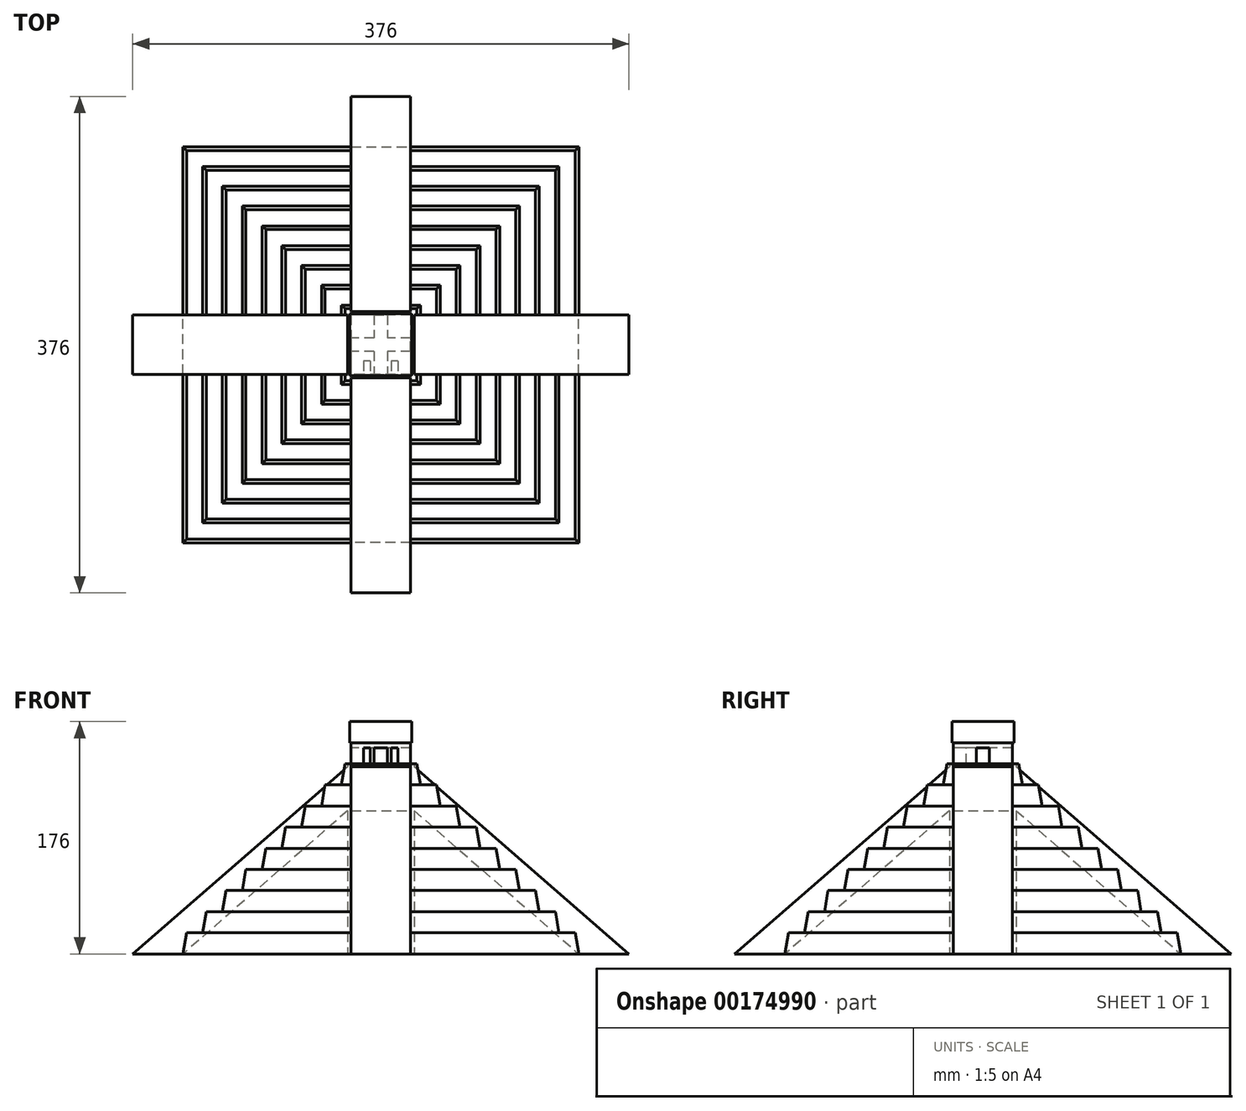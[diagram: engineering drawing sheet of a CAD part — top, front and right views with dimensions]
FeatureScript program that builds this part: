
annotation { "Feature Type Name" : "Feature", "Feature Type Description" : "" }
export const myFeature = defineFeature(function(context is Context, id is Id, definition is map)
    precondition{}
    {
        {
            var Q0;
            Q0=qCreatedBy(makeId("Top.planeOp"),FACE);
            var sketch = newSketch(context, id + "F0", { "sketchPlane" : qUnion([Q0])});
            skLineSegment(sketch, "E0.bottom", {"start": v(150, 150) * mm, "end": v(-150, 150) * mm});
            skLineSegment(sketch, "E0.top", {"start": v(150, -150) * mm, "end": v(-150, -150) * mm});
            skLineSegment(sketch, "E0.left", {"start": v(150, 150) * mm, "end": v(150, -150) * mm});
            skLineSegment(sketch, "E0.right", {"start": v(-150, 150) * mm, "end": v(-150, -150) * mm});
            skPoint(sketch, "E0.middle", {"position": v(0, 0) * mm});
            skSolve(sketch);
        }
        {
            var Q0;
            Q0=makeQuery(id+"F0.imprint","IMPRINT",FACE,{"disambiguationData":[TD([[makeQuery(id+"F0.imprint","IMPRINT",EDGE,{"derivedFrom":sQuery(id+"F0.wireOp",EDGE,"E0.bottom")}),1.0]])]});
            extrude(context, id + "F1", {"entities" : qUnion([Q0]), "depth" : 16 * mm, "hasDraft" : true, "draftAngle" : 10 * degree, "draftPullDirection" : true});
        }
        {
            var Q0;
            Q0=makeQuery(id+"F1.opExtrude","CAP_FACE",FACE,{"disambiguationData":[OSD([sQuery(id+"F0.wireOp",EDGE,"E0.bottom"),sQuery(id+"F0.wireOp",EDGE,"E0.top"),sQuery(id+"F0.wireOp",EDGE,"E0.left"),sQuery(id+"F0.wireOp",EDGE,"E0.right")])],"isStart":false});
            var sketch = newSketch(context, id + "F2", { "sketchPlane" : qUnion([Q0])});
            skLineSegment(sketch, "E1.bottom", {"start": v(135, 135) * mm, "end": v(-135, 135) * mm});
            skLineSegment(sketch, "E1.top", {"start": v(135, -135) * mm, "end": v(-135, -135) * mm});
            skLineSegment(sketch, "E1.left", {"start": v(135, 135) * mm, "end": v(135, -135) * mm});
            skLineSegment(sketch, "E1.right", {"start": v(-135, 135) * mm, "end": v(-135, -135) * mm});
            skPoint(sketch, "E1.middle", {"position": v(0, 0) * mm});
            skSolve(sketch);
        }
        {
            var Q0;
            Q0=makeQuery(id+"F2.imprint","IMPRINT",FACE,{"disambiguationData":[TD([[makeQuery(id+"F2.imprint","IMPRINT",EDGE,{"derivedFrom":sQuery(id+"F2.wireOp",EDGE,"E1.bottom")}),1.0]])]});
            extrude(context, id + "F3", {"entities" : qUnion([Q0]), "operationType" : NewBodyOperationType.ADD, "depth" : 16 * mm, "hasDraft" : true, "draftAngle" : 10 * degree, "draftPullDirection" : true});
        }
        {
            var Q0;
            Q0=makeQuery(id+"F3.opExtrude","CAP_FACE",FACE,{"disambiguationData":[OSD([sQuery(id+"F2.wireOp",EDGE,"E1.bottom"),sQuery(id+"F2.wireOp",EDGE,"E1.top"),sQuery(id+"F2.wireOp",EDGE,"E1.left"),sQuery(id+"F2.wireOp",EDGE,"E1.right")])],"isStart":false});
            var sketch = newSketch(context, id + "F4", { "sketchPlane" : qUnion([Q0])});
            skLineSegment(sketch, "E2.bottom", {"start": v(120, 120) * mm, "end": v(-120, 120) * mm});
            skLineSegment(sketch, "E2.top", {"start": v(120, -120) * mm, "end": v(-120, -120) * mm});
            skLineSegment(sketch, "E2.left", {"start": v(120, 120) * mm, "end": v(120, -120) * mm});
            skLineSegment(sketch, "E2.right", {"start": v(-120, 120) * mm, "end": v(-120, -120) * mm});
            skPoint(sketch, "E2.middle", {"position": v(0, 0) * mm});
            skSolve(sketch);
        }
        {
            var Q0;
            Q0=makeQuery(id+"F4.imprint","IMPRINT",FACE,{"disambiguationData":[TD([[makeQuery(id+"F4.imprint","IMPRINT",EDGE,{"derivedFrom":sQuery(id+"F4.wireOp",EDGE,"E2.bottom")}),1.0]])]});
            extrude(context, id + "F5", {"entities" : qUnion([Q0]), "operationType" : NewBodyOperationType.ADD, "depth" : 16 * mm, "hasDraft" : true, "draftAngle" : 10 * degree, "draftPullDirection" : true});
        }
        {
            var Q0;
            Q0=makeQuery(id+"F5.opExtrude","CAP_FACE",FACE,{"disambiguationData":[OSD([sQuery(id+"F4.wireOp",EDGE,"E2.bottom"),sQuery(id+"F4.wireOp",EDGE,"E2.top"),sQuery(id+"F4.wireOp",EDGE,"E2.left"),sQuery(id+"F4.wireOp",EDGE,"E2.right")])],"isStart":false});
            var sketch = newSketch(context, id + "F6", { "sketchPlane" : qUnion([Q0])});
            skLineSegment(sketch, "E3.bottom", {"start": v(105, 105) * mm, "end": v(-105, 105) * mm});
            skLineSegment(sketch, "E3.top", {"start": v(105, -105) * mm, "end": v(-105, -105) * mm});
            skLineSegment(sketch, "E3.left", {"start": v(105, 105) * mm, "end": v(105, -105) * mm});
            skLineSegment(sketch, "E3.right", {"start": v(-105, 105) * mm, "end": v(-105, -105) * mm});
            skPoint(sketch, "E3.middle", {"position": v(0, 0) * mm});
            skSolve(sketch);
        }
        {
            var Q0;
            Q0=makeQuery(id+"F6.imprint","IMPRINT",FACE,{"disambiguationData":[TD([[makeQuery(id+"F6.imprint","IMPRINT",EDGE,{"derivedFrom":sQuery(id+"F6.wireOp",EDGE,"E3.bottom")}),1.0]])]});
            extrude(context, id + "F7", {"entities" : qUnion([Q0]), "operationType" : NewBodyOperationType.ADD, "depth" : 16 * mm, "hasDraft" : true, "draftAngle" : 10 * degree, "draftPullDirection" : true});
        }
        {
            var Q0;
            Q0=makeQuery(id+"F7.opExtrude","CAP_FACE",FACE,{"disambiguationData":[OSD([sQuery(id+"F6.wireOp",EDGE,"E3.bottom"),sQuery(id+"F6.wireOp",EDGE,"E3.top"),sQuery(id+"F6.wireOp",EDGE,"E3.left"),sQuery(id+"F6.wireOp",EDGE,"E3.right")])],"isStart":false});
            var sketch = newSketch(context, id + "F8", { "sketchPlane" : qUnion([Q0])});
            skLineSegment(sketch, "E4.bottom", {"start": v(90, 90) * mm, "end": v(-90, 90) * mm});
            skLineSegment(sketch, "E4.top", {"start": v(90, -90) * mm, "end": v(-90, -90) * mm});
            skLineSegment(sketch, "E4.left", {"start": v(90, 90) * mm, "end": v(90, -90) * mm});
            skLineSegment(sketch, "E4.right", {"start": v(-90, 90) * mm, "end": v(-90, -90) * mm});
            skPoint(sketch, "E4.middle", {"position": v(0, 0) * mm});
            skSolve(sketch);
        }
        {
            var Q0;
            Q0=makeQuery(id+"F8.imprint","IMPRINT",FACE,{"disambiguationData":[TD([[makeQuery(id+"F8.imprint","IMPRINT",EDGE,{"derivedFrom":sQuery(id+"F8.wireOp",EDGE,"E4.bottom")}),1.0]])]});
            extrude(context, id + "F9", {"entities" : qUnion([Q0]), "operationType" : NewBodyOperationType.ADD, "depth" : 16 * mm, "hasDraft" : true, "draftAngle" : 10 * degree, "draftPullDirection" : true});
        }
        {
            var Q0;
            Q0=makeQuery(id+"F9.opExtrude","CAP_FACE",FACE,{"disambiguationData":[OSD([sQuery(id+"F8.wireOp",EDGE,"E4.bottom"),sQuery(id+"F8.wireOp",EDGE,"E4.top"),sQuery(id+"F8.wireOp",EDGE,"E4.left"),sQuery(id+"F8.wireOp",EDGE,"E4.right")])],"isStart":false});
            var sketch = newSketch(context, id + "F10", { "sketchPlane" : qUnion([Q0])});
            skLineSegment(sketch, "E5.bottom", {"start": v(75, 75) * mm, "end": v(-75, 75) * mm});
            skLineSegment(sketch, "E5.top", {"start": v(75, -75) * mm, "end": v(-75, -75) * mm});
            skLineSegment(sketch, "E5.left", {"start": v(75, 75) * mm, "end": v(75, -75) * mm});
            skLineSegment(sketch, "E5.right", {"start": v(-75, 75) * mm, "end": v(-75, -75) * mm});
            skPoint(sketch, "E5.middle", {"position": v(0, 0) * mm});
            skSolve(sketch);
        }
        {
            var Q0;
            Q0=makeQuery(id+"F10.imprint","IMPRINT",FACE,{"disambiguationData":[TD([[makeQuery(id+"F10.imprint","IMPRINT",EDGE,{"derivedFrom":sQuery(id+"F10.wireOp",EDGE,"E5.bottom")}),1.0]])]});
            extrude(context, id + "F11", {"entities" : qUnion([Q0]), "operationType" : NewBodyOperationType.ADD, "depth" : 16 * mm, "hasDraft" : true, "draftAngle" : 10 * degree, "draftPullDirection" : true});
        }
        {
            var Q0;
            Q0=makeQuery(id+"F11.opExtrude","CAP_FACE",FACE,{"disambiguationData":[OSD([sQuery(id+"F10.wireOp",EDGE,"E5.bottom"),sQuery(id+"F10.wireOp",EDGE,"E5.top"),sQuery(id+"F10.wireOp",EDGE,"E5.left"),sQuery(id+"F10.wireOp",EDGE,"E5.right")])],"isStart":false});
            var sketch = newSketch(context, id + "F12", { "sketchPlane" : qUnion([Q0])});
            skLineSegment(sketch, "E6.bottom", {"start": v(60, 60) * mm, "end": v(-60, 60) * mm});
            skLineSegment(sketch, "E6.top", {"start": v(60, -60) * mm, "end": v(-60, -60) * mm});
            skLineSegment(sketch, "E6.left", {"start": v(60, 60) * mm, "end": v(60, -60) * mm});
            skLineSegment(sketch, "E6.right", {"start": v(-60, 60) * mm, "end": v(-60, -60) * mm});
            skPoint(sketch, "E6.middle", {"position": v(0, 0) * mm});
            skSolve(sketch);
        }
        {
            var Q0;
            Q0=makeQuery(id+"F12.imprint","IMPRINT",FACE,{"disambiguationData":[TD([[makeQuery(id+"F12.imprint","IMPRINT",EDGE,{"derivedFrom":sQuery(id+"F12.wireOp",EDGE,"E6.bottom")}),1.0]])]});
            extrude(context, id + "F13", {"entities" : qUnion([Q0]), "operationType" : NewBodyOperationType.ADD, "depth" : 16 * mm, "hasDraft" : true, "draftAngle" : 10 * degree, "draftPullDirection" : true});
        }
        {
            var Q0;
            Q0=makeQuery(id+"F13.opExtrude","CAP_FACE",FACE,{"disambiguationData":[OSD([sQuery(id+"F12.wireOp",EDGE,"E6.bottom"),sQuery(id+"F12.wireOp",EDGE,"E6.top"),sQuery(id+"F12.wireOp",EDGE,"E6.left"),sQuery(id+"F12.wireOp",EDGE,"E6.right")])],"isStart":false});
            var sketch = newSketch(context, id + "F14", { "sketchPlane" : qUnion([Q0])});
            skLineSegment(sketch, "E7.bottom", {"start": v(45, 45) * mm, "end": v(-45, 45) * mm});
            skLineSegment(sketch, "E7.top", {"start": v(45, -45) * mm, "end": v(-45, -45) * mm});
            skLineSegment(sketch, "E7.left", {"start": v(45, 45) * mm, "end": v(45, -45) * mm});
            skLineSegment(sketch, "E7.right", {"start": v(-45, 45) * mm, "end": v(-45, -45) * mm});
            skPoint(sketch, "E7.middle", {"position": v(0, 0) * mm});
            skSolve(sketch);
        }
        {
            var Q0;
            Q0=makeQuery(id+"F14.imprint","IMPRINT",FACE,{"disambiguationData":[TD([[makeQuery(id+"F14.imprint","IMPRINT",EDGE,{"derivedFrom":sQuery(id+"F14.wireOp",EDGE,"E7.bottom")}),1.0]])]});
            extrude(context, id + "F15", {"entities" : qUnion([Q0]), "operationType" : NewBodyOperationType.ADD, "depth" : 16 * mm, "hasDraft" : true, "draftAngle" : 10 * degree, "draftPullDirection" : true});
        }
        {
            var Q0;
            Q0=makeQuery(id+"F15.opExtrude","CAP_FACE",FACE,{"disambiguationData":[OSD([sQuery(id+"F14.wireOp",EDGE,"E7.bottom"),sQuery(id+"F14.wireOp",EDGE,"E7.top"),sQuery(id+"F14.wireOp",EDGE,"E7.left"),sQuery(id+"F14.wireOp",EDGE,"E7.right")])],"isStart":false});
            var sketch = newSketch(context, id + "F16", { "sketchPlane" : qUnion([Q0])});
            skLineSegment(sketch, "E8.bottom", {"start": v(30, 30) * mm, "end": v(-30, 30) * mm});
            skLineSegment(sketch, "E8.top", {"start": v(30, -30) * mm, "end": v(-30, -30) * mm});
            skLineSegment(sketch, "E8.left", {"start": v(30, 30) * mm, "end": v(30, -30) * mm});
            skLineSegment(sketch, "E8.right", {"start": v(-30, 30) * mm, "end": v(-30, -30) * mm});
            skPoint(sketch, "E8.middle", {"position": v(0, 0) * mm});
            skSolve(sketch);
        }
        {
            var Q0;
            Q0=makeQuery(id+"F16.imprint","IMPRINT",FACE,{"disambiguationData":[TD([[makeQuery(id+"F16.imprint","IMPRINT",EDGE,{"derivedFrom":sQuery(id+"F16.wireOp",EDGE,"E8.bottom")}),1.0]])]});
            extrude(context, id + "F17", {"entities" : qUnion([Q0]), "operationType" : NewBodyOperationType.ADD, "depth" : 16 * mm, "hasDraft" : true, "draftAngle" : 10 * degree, "draftPullDirection" : true});
        }
        {
            var Q0;
            Q0=makeQuery(id+"F17.opExtrude","CAP_FACE",FACE,{"disambiguationData":[OSD([sQuery(id+"F16.wireOp",EDGE,"E8.bottom"),sQuery(id+"F16.wireOp",EDGE,"E8.top"),sQuery(id+"F16.wireOp",EDGE,"E8.left"),sQuery(id+"F16.wireOp",EDGE,"E8.right")])],"isStart":false});
            var sketch = newSketch(context, id + "F18", { "sketchPlane" : qUnion([Q0])});
            skLineSegment(sketch, "E9.bottom", {"start": v(150, 22.5) * mm, "end": v(-150, 22.5) * mm});
            skLineSegment(sketch, "E9.top", {"start": v(150, -22.5) * mm, "end": v(-150, -22.5) * mm});
            skLineSegment(sketch, "E9.left", {"start": v(150, 22.5) * mm, "end": v(150, -22.5) * mm});
            skLineSegment(sketch, "E9.right", {"start": v(-150, 22.5) * mm, "end": v(-150, -22.5) * mm});
            skPoint(sketch, "E9.middle", {"position": v(0, 0) * mm});
            skLineSegment(sketch, "E10.bottom", {"start": v(22.5, 150) * mm, "end": v(-22.5, 150) * mm});
            skLineSegment(sketch, "E10.top", {"start": v(22.5, -150) * mm, "end": v(-22.5, -150) * mm});
            skLineSegment(sketch, "E10.left", {"start": v(22.5, 150) * mm, "end": v(22.5, -150) * mm});
            skLineSegment(sketch, "E10.right", {"start": v(-22.5, 150) * mm, "end": v(-22.5, -150) * mm});
            skSolve(sketch);
        }
        {
            var Q0;
            Q0 = qSketchRegion(id + "F18", true);
            extrude(context, id + "F19", {"entities" : qUnion([Q0]), "operationType" : NewBodyOperationType.REMOVE, "endBound" : BoundingType.THROUGH_ALL, "oppositeDirection" : true, "depth" : 25 * mm});
        }
        {
            var Q0;
            Q0=qCreatedBy(makeId("Top.planeOp"),FACE);
            var sketch = newSketch(context, id + "F20", { "sketchPlane" : qUnion([Q0])});
            skLineSegment(sketch, "E11.bottom", {"start": v(22.5, 188) * mm, "end": v(-22.5, 188) * mm});
            skLineSegment(sketch, "E11.top", {"start": v(22.5, -188) * mm, "end": v(-22.5, -188) * mm});
            skLineSegment(sketch, "E11.left", {"start": v(22.5, 188) * mm, "end": v(22.5, -188) * mm});
            skLineSegment(sketch, "E11.right", {"start": v(-22.5, 188) * mm, "end": v(-22.5, -188) * mm});
            skPoint(sketch, "E11.middle", {"position": v(0, 0) * mm});
            skLineSegment(sketch, "E12.bottom", {"start": v(188, 22.5) * mm, "end": v(-188, 22.5) * mm});
            skLineSegment(sketch, "E12.top", {"start": v(188, -22.5) * mm, "end": v(-188, -22.5) * mm});
            skLineSegment(sketch, "E12.left", {"start": v(188, 22.5) * mm, "end": v(188, -22.5) * mm});
            skLineSegment(sketch, "E12.right", {"start": v(-188, 22.5) * mm, "end": v(-188, -22.5) * mm});
            skSolve(sketch);
        }
        {
            var Q0;
            Q0=qCreatedBy(makeId("Front.planeOp"),FACE);
            var sketch = newSketch(context, id + "F21", { "sketchPlane" : qUnion([Q0])});
            skLineSegment(sketch, "E13", {"start": v(22.5, 144) * mm, "end": v(188, 0) * mm});
            skLineSegment(sketch, "E14", {"start": v(22.5, 0) * mm, "end": v(188, 0) * mm});
            skSolve(sketch);
        }
        {
            var Q0;
            Q0=sQuery(id+"F21.wireOp",EDGE,"E13");
            cPoint(context, id + "F22", {"entities" : qUnion([Q0]), "parameter" : 0.5});
        }
        {
            var Q0;
            Q0=sQuery(id+"F21.wireOp",VERTEX,"E13.start");
            var Q1;
            Q1=sQuery(id+"F20.wireOp",VERTEX,"E12.bottom.start");
            var Q2;
            Q2 = qCreatedBy(id + "F22" ,VERTEX);
            cPlane(context, id + "F23", {"entities" : qUnion([Q0, Q1, Q2]), "cplaneType" : CPlaneType.THREE_POINT, "offset" : 25 * mm, "width" : 150 * mm, "height" : 150 * mm});
        }
        {
            var Q0;
            Q0=qCreatedBy(id+"F23.planeOp",FACE);
            var sketch = newSketch(context, id + "F24", { "sketchPlane" : qUnion([Q0])});
            skLineSegment(sketch, "E15.bottom", {"start": v(-74.02, -22.5) * mm, "end": v(141.83, -22.5) * mm});
            skLineSegment(sketch, "E15.top", {"start": v(-74.02, 22.5) * mm, "end": v(141.83, 22.5) * mm});
            skLineSegment(sketch, "E15.left", {"start": v(-74.02, -22.5) * mm, "end": v(-74.02, 22.5) * mm});
            skLineSegment(sketch, "E15.right", {"start": v(141.83, -22.5) * mm, "end": v(141.83, 22.5) * mm});
            skSolve(sketch);
        }
        {
            var Q0;
            Q0 = qSketchRegion(id + "F24", true);
            extrude(context, id + "F25", {"entities" : qUnion([Q0]), "oppositeDirection" : true, "depth" : 25 * mm});
        }
        {
            var Q0;
            Q0=qCreatedBy(makeId("Front.planeOp"),FACE);
            var sketch = newSketch(context, id + "F26", { "sketchPlane" : qUnion([Q0])});
            skLineSegment(sketch, "E16", {"start": v(-22.5, 144) * mm, "end": v(-188, 0) * mm});
            skSolve(sketch);
        }
        {
            var Q0;
            Q0=qCreatedBy(makeId("Right.planeOp"),FACE);
            var sketch = newSketch(context, id + "F27", { "sketchPlane" : qUnion([Q0])});
            skLineSegment(sketch, "E17", {"start": v(-22.5, 144) * mm, "end": v(-188, 0) * mm});
            skLineSegment(sketch, "E18", {"start": v(188, 0) * mm, "end": v(22.5, 144) * mm});
            skSolve(sketch);
        }
        {
            var Q0;
            Q0=sQuery(id+"F27.wireOp",EDGE,"E18");
            cPoint(context, id + "F28", {"entities" : qUnion([Q0]), "parameter" : 0.5});
        }
        {
            var Q0;
            Q0=sQuery(id+"F27.wireOp",VERTEX,"E18.end");
            var Q1;
            Q1=sQuery(id+"F20.wireOp",VERTEX,"E11.right.start");
            var Q2;
            Q2 = qCreatedBy(id + "F28" ,VERTEX);
            cPlane(context, id + "F29", {"entities" : qUnion([Q0, Q1, Q2]), "cplaneType" : CPlaneType.THREE_POINT, "offset" : 25 * mm, "width" : 150 * mm, "height" : 150 * mm});
        }
        {
            var Q0;
            Q0=sQuery(id+"F27.wireOp",EDGE,"E17");
            cPoint(context, id + "F30", {"entities" : qUnion([Q0]), "parameter" : 0.5});
        }
        {
            var Q0;
            Q0=sQuery(id+"F27.wireOp",VERTEX,"E17.start");
            var Q1;
            Q1=sQuery(id+"F20.wireOp",VERTEX,"E11.right.end");
            var Q2;
            Q2 = qCreatedBy(id + "F30" ,VERTEX);
            cPlane(context, id + "F31", {"entities" : qUnion([Q0, Q1, Q2]), "cplaneType" : CPlaneType.THREE_POINT, "offset" : 25 * mm, "width" : 150 * mm, "height" : 150 * mm});
        }
        {
            var Q0;
            Q0=sQuery(id+"F26.wireOp",EDGE,"E16");
            cPoint(context, id + "F32", {"entities" : qUnion([Q0]), "parameter" : 0.5});
        }
        {
            var Q0;
            Q0=sQuery(id+"F26.wireOp",VERTEX,"E16.start");
            var Q1;
            Q1 = qCreatedBy(id + "F32" ,VERTEX);
            var Q2;
            Q2=sQuery(id+"F20.wireOp",VERTEX,"E12.top.end");
            cPlane(context, id + "F33", {"entities" : qUnion([Q0, Q1, Q2]), "cplaneType" : CPlaneType.THREE_POINT, "offset" : 25 * mm, "width" : 150 * mm, "height" : 150 * mm});
        }
        {
            var Q0;
            Q0=makeQuery(id+"F25.opExtrude","SWEPT_FACE",FACE,{"disambiguationData":[OSD([sQuery(id+"F24.wireOp",EDGE,"E15.top")])]});
            var sketch = newSketch(context, id + "F34", { "sketchPlane" : qUnion([Q0])});
            skLineSegment(sketch, "E19", {"start": v(-22.5, 138.62) * mm, "end": v(-8.75, 122.82) * mm});
            skLineSegment(sketch, "E20", {"start": v(-8.75, 122.82) * mm, "end": v(-22.5, 110.86) * mm});
            skLineSegment(sketch, "E21", {"start": v(-22.5, 138.62) * mm, "end": v(-22.5, 110.86) * mm});
            skLineSegment(sketch, "E22", {"start": v(-149.91, 0) * mm, "end": v(-188, 0) * mm});
            skLineSegment(sketch, "E23", {"start": v(-188, 0) * mm, "end": v(-171.59, -18.86) * mm});
            skLineSegment(sketch, "E24", {"start": v(-171.59, -18.86) * mm, "end": v(-149.91, 0) * mm});
            skSolve(sketch);
        }
        {
            var Q0;
            Q0=makeQuery(id+"F34.imprint","IMPRINT",FACE,{"disambiguationData":[TD([[makeQuery(id+"F34.imprint","IMPRINT",EDGE,{"derivedFrom":sQuery(id+"F34.wireOp",EDGE,"E19")}),1.0]])]});
            var Q1;
            Q1=makeQuery(id+"F34.imprint","IMPRINT",FACE,{"disambiguationData":[TD([[makeQuery(id+"F34.imprint","IMPRINT",EDGE,{"derivedFrom":sQuery(id+"F34.wireOp",EDGE,"E22")}),1.0]])]});
            extrude(context, id + "F35", {"entities" : qUnion([Q0, Q1]), "operationType" : NewBodyOperationType.REMOVE, "endBound" : BoundingType.THROUGH_ALL, "oppositeDirection" : true, "depth" : 25 * mm});
        }
        {
            var Q0;
            Q0=qCreatedBy(id+"F29.planeOp",FACE);
            var sketch = newSketch(context, id + "F36", { "sketchPlane" : qUnion([Q0])});
            skLineSegment(sketch, "E25.bottom", {"start": v(22.5, -74.02) * mm, "end": v(-22.5, -74.02) * mm});
            skLineSegment(sketch, "E25.top", {"start": v(22.5, 141.83) * mm, "end": v(-22.5, 141.83) * mm});
            skLineSegment(sketch, "E25.left", {"start": v(22.5, -74.02) * mm, "end": v(22.5, 141.83) * mm});
            skLineSegment(sketch, "E25.right", {"start": v(-22.5, -74.02) * mm, "end": v(-22.5, 141.83) * mm});
            skSolve(sketch);
        }
        {
            var Q0;
            Q0 = qSketchRegion(id + "F36", true);
            extrude(context, id + "F37", {"entities" : qUnion([Q0]), "oppositeDirection" : true, "depth" : 25 * mm});
        }
        {
            var Q0;
            Q0=makeQuery(id+"F37.opExtrude","SWEPT_FACE",FACE,{"disambiguationData":[OSD([sQuery(id+"F36.wireOp",EDGE,"E25.left")])]});
            var sketch = newSketch(context, id + "F38", { "sketchPlane" : qUnion([Q0])});
            skLineSegment(sketch, "E26", {"start": v(188, 0) * mm, "end": v(171.59, -18.86) * mm});
            skLineSegment(sketch, "E27", {"start": v(171.59, -18.86) * mm, "end": v(149.91, 0) * mm});
            skLineSegment(sketch, "E28", {"start": v(149.91, 0) * mm, "end": v(188, 0) * mm});
            skSolve(sketch);
        }
        {
            var Q0;
            Q0=makeQuery(id+"F38.imprint","IMPRINT",FACE,{"disambiguationData":[TD([[makeQuery(id+"F38.imprint","IMPRINT",EDGE,{"derivedFrom":sQuery(id+"F38.wireOp",EDGE,"E26")}),1.0]])]});
            extrude(context, id + "F39", {"entities" : qUnion([Q0]), "operationType" : NewBodyOperationType.REMOVE, "endBound" : BoundingType.THROUGH_ALL, "oppositeDirection" : true, "depth" : 25 * mm});
        }
        {
            var Q0;
            {var subQ0=sQuery(id+"F16.wireOp",EDGE,"E8.bottom");var subQ1=sQuery(id+"F16.wireOp",EDGE,"E8.left");var subQ2=sQuery(id+"F18.wireOp",EDGE,"E10.left");var subQ3=sQuery(id+"F18.wireOp",EDGE,"E9.bottom");var subQ4=makeQuery(id+"F18.imprint","INTERSECT",VERTEX,{"derivedFrom":[subQ3,subQ2]});Q0=makeQuery(id+"F19.boolean.opBoolean","SPLIT",FACE,{"disambiguationData":[TD([makeQuery(id+"F19.opExtrude","SWEPT_FACE",FACE,{"disambiguationData":[OSD([subQ3]),TDD([makeQuery(id+"F18.imprint","IMPRINT",EDGE,{"disambiguationData":[TD([[makeQuery(id+"F18.imprint","INTERSECT",VERTEX,{"derivedFrom":[subQ3,sQuery(id+"F18.wireOp",EDGE,"E9.left")]}),-1.0]])],"derivedFrom":subQ3}),makeQuery(id+"F18.imprint","IMPRINT",EDGE,{"disambiguationData":[TD([[subQ4,1.0]])],"derivedFrom":subQ3})])]})])],"derivedFrom":makeQuery(id+"F17.opExtrude","CAP_FACE",FACE,{"disambiguationData":[OSD([subQ0,sQuery(id+"F16.wireOp",EDGE,"E8.top"),subQ1,sQuery(id+"F16.wireOp",EDGE,"E8.right")])],"isStart":false})});}
            var sketch = newSketch(context, id + "F40", { "sketchPlane" : qUnion([Q0])});
            skLineSegment(sketch, "E29.bottom", {"start": v(22.5, 8.75) * mm, "end": v(-22.5, 8.75) * mm});
            skLineSegment(sketch, "E29.top", {"start": v(22.5, 25.16) * mm, "end": v(-22.5, 25.16) * mm});
            skLineSegment(sketch, "E29.left", {"start": v(22.5, 8.75) * mm, "end": v(22.5, 25.16) * mm});
            skLineSegment(sketch, "E29.right", {"start": v(-22.5, 8.75) * mm, "end": v(-22.5, 25.16) * mm});
            skSolve(sketch);
        }
        {
            var Q0;
            Q0 = qSketchRegion(id + "F40", true);
            extrude(context, id + "F41", {"entities" : qUnion([Q0]), "operationType" : NewBodyOperationType.REMOVE, "endBound" : BoundingType.THROUGH_ALL, "oppositeDirection" : true, "depth" : 25 * mm});
        }
        {
            var Q0;
            Q0=qCreatedBy(id+"F31.planeOp",FACE);
            var sketch = newSketch(context, id + "F42", { "sketchPlane" : qUnion([Q0])});
            skLineSegment(sketch, "E30.bottom", {"start": v(-22.5, -74.02) * mm, "end": v(22.5, -74.02) * mm});
            skLineSegment(sketch, "E30.top", {"start": v(-22.5, 141.83) * mm, "end": v(22.5, 141.83) * mm});
            skLineSegment(sketch, "E30.left", {"start": v(-22.5, -74.02) * mm, "end": v(-22.5, 141.83) * mm});
            skLineSegment(sketch, "E30.right", {"start": v(22.5, -74.02) * mm, "end": v(22.5, 141.83) * mm});
            skSolve(sketch);
        }
        {
            var Q0;
            Q0 = qSketchRegion(id + "F42", true);
            extrude(context, id + "F43", {"entities" : qUnion([Q0]), "depth" : 25 * mm});
        }
        {
            var Q0;
            Q0=qCreatedBy(id+"F33.planeOp",FACE);
            var sketch = newSketch(context, id + "F44", { "sketchPlane" : qUnion([Q0])});
            skLineSegment(sketch, "E31.bottom", {"start": v(74.02, -22.5) * mm, "end": v(-141.83, -22.5) * mm});
            skLineSegment(sketch, "E31.top", {"start": v(74.02, 22.5) * mm, "end": v(-141.83, 22.5) * mm});
            skLineSegment(sketch, "E31.left", {"start": v(74.02, -22.5) * mm, "end": v(74.02, 22.5) * mm});
            skLineSegment(sketch, "E31.right", {"start": v(-141.83, -22.5) * mm, "end": v(-141.83, 22.5) * mm});
            skSolve(sketch);
        }
        {
            var Q0;
            Q0 = qSketchRegion(id + "F44", true);
            extrude(context, id + "F45", {"entities" : qUnion([Q0]), "depth" : 25 * mm});
        }
        {
            var Q0;
            Q0=makeQuery(id+"F43.opExtrude","SWEPT_FACE",FACE,{"disambiguationData":[OSD([sQuery(id+"F42.wireOp",EDGE,"E30.left")])]});
            var sketch = newSketch(context, id + "F46", { "sketchPlane" : qUnion([Q0])});
            skLineSegment(sketch, "E32", {"start": v(188, 0) * mm, "end": v(171.59, -18.86) * mm});
            skLineSegment(sketch, "E33", {"start": v(171.59, -18.86) * mm, "end": v(149.91, 0) * mm});
            skLineSegment(sketch, "E34", {"start": v(149.91, 0) * mm, "end": v(188, 0) * mm});
            skSolve(sketch);
        }
        {
            var Q0;
            Q0=makeQuery(id+"F46.imprint","IMPRINT",FACE,{"disambiguationData":[TD([[makeQuery(id+"F46.imprint","IMPRINT",EDGE,{"derivedFrom":sQuery(id+"F46.wireOp",EDGE,"E32")}),1.0]])]});
            extrude(context, id + "F47", {"entities" : qUnion([Q0]), "operationType" : NewBodyOperationType.REMOVE, "endBound" : BoundingType.THROUGH_ALL, "oppositeDirection" : true, "depth" : 25 * mm});
        }
        {
            var Q0;
            Q0=makeQuery(id+"F45.opExtrude","SWEPT_FACE",FACE,{"disambiguationData":[OSD([sQuery(id+"F44.wireOp",EDGE,"E31.bottom")])]});
            var sketch = newSketch(context, id + "F48", { "sketchPlane" : qUnion([Q0])});
            skLineSegment(sketch, "E35", {"start": v(188, 0) * mm, "end": v(171.59, -18.86) * mm});
            skLineSegment(sketch, "E36", {"start": v(171.59, -18.86) * mm, "end": v(149.91, 0) * mm});
            skLineSegment(sketch, "E37", {"start": v(149.91, 0) * mm, "end": v(188, 0) * mm});
            skSolve(sketch);
        }
        {
            var Q0;
            Q0=makeQuery(id+"F48.imprint","IMPRINT",FACE,{"disambiguationData":[TD([[makeQuery(id+"F48.imprint","IMPRINT",EDGE,{"derivedFrom":sQuery(id+"F48.wireOp",EDGE,"E35")}),1.0]])]});
            extrude(context, id + "F49", {"entities" : qUnion([Q0]), "operationType" : NewBodyOperationType.REMOVE, "endBound" : BoundingType.THROUGH_ALL, "oppositeDirection" : true, "depth" : 25 * mm});
        }
        {
            var Q0;
            {var subQ0=sQuery(id+"F16.wireOp",EDGE,"E8.top");var subQ1=sQuery(id+"F16.wireOp",EDGE,"E8.left");var subQ2=sQuery(id+"F18.wireOp",EDGE,"E10.left");var subQ3=sQuery(id+"F18.wireOp",EDGE,"E9.top");var subQ4=makeQuery(id+"F18.imprint","INTERSECT",VERTEX,{"derivedFrom":[subQ3,subQ2]});Q0=makeQuery(id+"F19.boolean.opBoolean","SPLIT",FACE,{"disambiguationData":[TD([makeQuery(id+"F19.opExtrude","SWEPT_FACE",FACE,{"disambiguationData":[OSD([subQ3]),TDD([makeQuery(id+"F18.imprint","IMPRINT",EDGE,{"disambiguationData":[TD([[makeQuery(id+"F18.imprint","INTERSECT",VERTEX,{"derivedFrom":[subQ3,sQuery(id+"F18.wireOp",EDGE,"E9.left")]}),-1.0]])],"derivedFrom":subQ3}),makeQuery(id+"F18.imprint","IMPRINT",EDGE,{"disambiguationData":[TD([[subQ4,1.0]])],"derivedFrom":subQ3})])]})])],"derivedFrom":makeQuery(id+"F17.opExtrude","CAP_FACE",FACE,{"disambiguationData":[OSD([sQuery(id+"F16.wireOp",EDGE,"E8.bottom"),subQ0,subQ1,sQuery(id+"F16.wireOp",EDGE,"E8.right")])],"isStart":false})});}
            var sketch = newSketch(context, id + "F50", { "sketchPlane" : qUnion([Q0])});
            skLineSegment(sketch, "E38.bottom", {"start": v(22.5, -25.16) * mm, "end": v(-22.5, -25.16) * mm});
            skLineSegment(sketch, "E38.top", {"start": v(22.5, -8.75) * mm, "end": v(-8.75, -8.75) * mm});
            skLineSegment(sketch, "E38.left", {"start": v(22.5, -25.16) * mm, "end": v(22.5, -8.75) * mm});
            skLineSegment(sketch, "E38.right", {"start": v(-22.5, -25.16) * mm, "end": v(-22.5, -22.5) * mm});
            skLineSegment(sketch, "E39.bottom", {"start": v(-22.5, -22.5) * mm, "end": v(-25.16, -22.5) * mm});
            skLineSegment(sketch, "E39.top", {"start": v(-8.75, 22.5) * mm, "end": v(-25.16, 22.5) * mm});
            skLineSegment(sketch, "E39.left", {"start": v(-8.75, -8.75) * mm, "end": v(-8.75, 22.5) * mm});
            skLineSegment(sketch, "E39.right", {"start": v(-25.16, -22.5) * mm, "end": v(-25.16, 22.5) * mm});
            skSolve(sketch);
        }
        {
            var Q0;
            Q0 = qSketchRegion(id + "F50", true);
            extrude(context, id + "F51", {"entities" : qUnion([Q0]), "operationType" : NewBodyOperationType.REMOVE, "endBound" : BoundingType.THROUGH_ALL, "oppositeDirection" : true, "depth" : 25 * mm});
        }
        {
            var Q0;
            {var subQ0=sQuery(id+"F16.wireOp",EDGE,"E8.top");var subQ1=sQuery(id+"F16.wireOp",EDGE,"E8.left");var subQ2=sQuery(id+"F18.wireOp",EDGE,"E10.left");var subQ3=sQuery(id+"F18.wireOp",EDGE,"E9.top");var subQ4=makeQuery(id+"F18.imprint","INTERSECT",VERTEX,{"derivedFrom":[subQ3,subQ2]});Q0=makeQuery(id+"F19.boolean.opBoolean","SPLIT",FACE,{"disambiguationData":[TD([makeQuery(id+"F19.opExtrude","SWEPT_FACE",FACE,{"disambiguationData":[OSD([subQ3]),TDD([makeQuery(id+"F18.imprint","IMPRINT",EDGE,{"disambiguationData":[TD([[makeQuery(id+"F18.imprint","INTERSECT",VERTEX,{"derivedFrom":[subQ3,sQuery(id+"F18.wireOp",EDGE,"E9.left")]}),-1.0]])],"derivedFrom":subQ3}),makeQuery(id+"F18.imprint","IMPRINT",EDGE,{"disambiguationData":[TD([[subQ4,1.0]])],"derivedFrom":subQ3})])]})])],"derivedFrom":makeQuery(id+"F17.opExtrude","CAP_FACE",FACE,{"disambiguationData":[OSD([sQuery(id+"F16.wireOp",EDGE,"E8.bottom"),subQ0,subQ1,sQuery(id+"F16.wireOp",EDGE,"E8.right")])],"isStart":false})});}
            var sketch = newSketch(context, id + "F52", { "sketchPlane" : qUnion([Q0])});
            skLineSegment(sketch, "E40.bottom", {"start": v(25.16, -22.5) * mm, "end": v(22.5, -22.5) * mm});
            skLineSegment(sketch, "E40.top", {"start": v(25.16, 22.5) * mm, "end": v(22.5, 22.5) * mm});
            skLineSegment(sketch, "E40.left", {"start": v(25.16, -22.5) * mm, "end": v(25.16, 22.5) * mm});
            skLineSegment(sketch, "E40.right", {"start": v(22.5, -22.5) * mm, "end": v(22.5, 22.5) * mm});
            skSolve(sketch);
        }
        {
            var Q0;
            Q0 = qSketchRegion(id + "F52", true);
            extrude(context, id + "F53", {"entities" : qUnion([Q0]), "operationType" : NewBodyOperationType.REMOVE, "endBound" : BoundingType.THROUGH_ALL, "oppositeDirection" : true, "depth" : 25 * mm});
        }
        {
            var Q0;
            Q0=qCreatedBy(makeId("Top.planeOp"),FACE);
            var sketch = newSketch(context, id + "F54", { "sketchPlane" : qUnion([Q0])});
            skLineSegment(sketch, "E41.bottom", {"start": v(22.5, -25.16) * mm, "end": v(-22.5, -25.16) * mm});
            skLineSegment(sketch, "E41.top", {"start": v(22.5, 25.16) * mm, "end": v(-22.5, 25.16) * mm});
            skLineSegment(sketch, "E41.left", {"start": v(22.5, -25.16) * mm, "end": v(22.5, 25.16) * mm});
            skLineSegment(sketch, "E41.right", {"start": v(-22.5, -25.16) * mm, "end": v(-22.5, 25.16) * mm});
            skLineSegment(sketch, "E42.bottom", {"start": v(25.16, -22.5) * mm, "end": v(-25.16, -22.5) * mm});
            skLineSegment(sketch, "E42.top", {"start": v(25.16, 22.5) * mm, "end": v(-25.16, 22.5) * mm});
            skLineSegment(sketch, "E42.left", {"start": v(25.16, -22.5) * mm, "end": v(25.16, 22.5) * mm});
            skLineSegment(sketch, "E42.right", {"start": v(-25.16, -22.5) * mm, "end": v(-25.16, 22.5) * mm});
            skSolve(sketch);
        }
        {
            var Q0;
            Q0 = qSketchRegion(id + "F54", true);
            extrude(context, id + "F55", {"entities" : qUnion([Q0]), "depth" : 144 * mm});
        }
        {
            var Q0;
            Q0=makeQuery(id+"F19.boolean.opBoolean","SPLIT",BODY,{"disambiguationData":[OD(0.0)],"derivedFrom":makeQuery(id+"F1.opExtrude","SWEPT_BODY",BODY,{"disambiguationData":[OSD([sQuery(id+"F0.wireOp",EDGE,"E0.bottom"),sQuery(id+"F0.wireOp",EDGE,"E0.top"),sQuery(id+"F0.wireOp",EDGE,"E0.left"),sQuery(id+"F0.wireOp",EDGE,"E0.right")])]})});
            var Q1;
            Q1=makeQuery(id+"F19.boolean.opBoolean","SPLIT",BODY,{"disambiguationData":[OD(1.0)],"derivedFrom":makeQuery(id+"F1.opExtrude","SWEPT_BODY",BODY,{"disambiguationData":[OSD([sQuery(id+"F0.wireOp",EDGE,"E0.bottom"),sQuery(id+"F0.wireOp",EDGE,"E0.top"),sQuery(id+"F0.wireOp",EDGE,"E0.left"),sQuery(id+"F0.wireOp",EDGE,"E0.right")])]})});
            var Q2;
            Q2=makeQuery(id+"F19.boolean.opBoolean","SPLIT",BODY,{"disambiguationData":[OD(2.0)],"derivedFrom":makeQuery(id+"F1.opExtrude","SWEPT_BODY",BODY,{"disambiguationData":[OSD([sQuery(id+"F0.wireOp",EDGE,"E0.bottom"),sQuery(id+"F0.wireOp",EDGE,"E0.top"),sQuery(id+"F0.wireOp",EDGE,"E0.left"),sQuery(id+"F0.wireOp",EDGE,"E0.right")])]})});
            var Q3;
            Q3=makeQuery(id+"F19.boolean.opBoolean","SPLIT",BODY,{"disambiguationData":[OD(3.0)],"derivedFrom":makeQuery(id+"F1.opExtrude","SWEPT_BODY",BODY,{"disambiguationData":[OSD([sQuery(id+"F0.wireOp",EDGE,"E0.bottom"),sQuery(id+"F0.wireOp",EDGE,"E0.top"),sQuery(id+"F0.wireOp",EDGE,"E0.left"),sQuery(id+"F0.wireOp",EDGE,"E0.right")])]})});
            var Q4;
            Q4=makeQuery(id+"F25.opExtrude","SWEPT_BODY",BODY,{"disambiguationData":[OSD([sQuery(id+"F24.wireOp",EDGE,"E15.bottom"),sQuery(id+"F24.wireOp",EDGE,"E15.top"),sQuery(id+"F24.wireOp",EDGE,"E15.left"),sQuery(id+"F24.wireOp",EDGE,"E15.right")])]});
            var Q5;
            Q5=makeQuery(id+"F43.opExtrude","SWEPT_BODY",BODY,{"disambiguationData":[OSD([sQuery(id+"F42.wireOp",EDGE,"E30.bottom"),sQuery(id+"F42.wireOp",EDGE,"E30.top"),sQuery(id+"F42.wireOp",EDGE,"E30.left"),sQuery(id+"F42.wireOp",EDGE,"E30.right")])]});
            var Q6;
            Q6=makeQuery(id+"F45.opExtrude","SWEPT_BODY",BODY,{"disambiguationData":[OSD([sQuery(id+"F44.wireOp",EDGE,"E31.bottom"),sQuery(id+"F44.wireOp",EDGE,"E31.top"),sQuery(id+"F44.wireOp",EDGE,"E31.left"),sQuery(id+"F44.wireOp",EDGE,"E31.right")])]});
            var Q7;
            Q7=makeQuery(id+"F55.opExtrude","SWEPT_BODY",BODY,{"disambiguationData":[OSD([sQuery(id+"F54.wireOp",EDGE,"E41.bottom"),sQuery(id+"F54.wireOp",EDGE,"E41.top"),sQuery(id+"F54.wireOp",EDGE,"E41.left"),sQuery(id+"F54.wireOp",EDGE,"E41.right"),sQuery(id+"F54.wireOp",EDGE,"E42.bottom"),sQuery(id+"F54.wireOp",EDGE,"E42.top"),sQuery(id+"F54.wireOp",EDGE,"E42.left"),sQuery(id+"F54.wireOp",EDGE,"E42.right")])]});
            var Q8;
            Q8=makeQuery(id+"F37.opExtrude","SWEPT_BODY",BODY,{"disambiguationData":[OSD([sQuery(id+"F36.wireOp",EDGE,"E25.bottom"),sQuery(id+"F36.wireOp",EDGE,"E25.top"),sQuery(id+"F36.wireOp",EDGE,"E25.left"),sQuery(id+"F36.wireOp",EDGE,"E25.right")])]});
            booleanBodies(context, id + "F56", {"operationType" : BooleanOperationType.UNION, "tools" : qUnion([Q0, Q1, Q2, Q3, Q4, Q5, Q6, Q7, Q8])});
        }
        {
            var Q0;
            {var subQ0=sQuery(id+"F16.wireOp",EDGE,"E8.top");var subQ2=sQuery(id+"F16.wireOp",EDGE,"E8.right");var subQ4=sQuery(id+"F18.wireOp",EDGE,"E9.right");var subQ5=sQuery(id+"F18.wireOp",EDGE,"E9.top");var subQ8=sQuery(id+"F18.wireOp",EDGE,"E10.right");var subQ9=makeQuery(id+"F18.imprint","INTERSECT",VERTEX,{"derivedFrom":[subQ5,subQ8]});var subQ13=sQuery(id+"F16.wireOp",EDGE,"E8.left");var subQ14=sQuery(id+"F16.wireOp",EDGE,"E8.bottom");var subQ15=makeQuery(id+"F17.opExtrude","CAP_FACE",FACE,{"disambiguationData":[OSD([subQ14,subQ0,subQ13,subQ2])],"isStart":false});var subQ17=sQuery(id+"F18.wireOp",EDGE,"E10.left");var subQ18=makeQuery(id+"F18.imprint","INTERSECT",VERTEX,{"derivedFrom":[subQ5,subQ17]});var subQ21=sQuery(id+"F18.wireOp",EDGE,"E9.left");var subQ24=sQuery(id+"F18.wireOp",EDGE,"E9.bottom");var subQ26=makeQuery(id+"F18.imprint","INTERSECT",VERTEX,{"derivedFrom":[subQ24,subQ8]});var subQ30=makeQuery(id+"F18.imprint","INTERSECT",VERTEX,{"derivedFrom":[subQ24,subQ17]});Q0=makeQuery(id+"F56.opBoolean","MERGE",FACE,{"derivedFrom":[makeQuery(id+"F19.boolean.opBoolean","SPLIT",FACE,{"disambiguationData":[TD([makeQuery(id+"F19.opExtrude","SWEPT_FACE",FACE,{"disambiguationData":[OSD([subQ24]),TDD([makeQuery(id+"F18.imprint","IMPRINT",EDGE,{"disambiguationData":[TD([[makeQuery(id+"F18.imprint","INTERSECT",VERTEX,{"derivedFrom":[subQ24,subQ21]}),-1.0]])],"derivedFrom":subQ24}),makeQuery(id+"F18.imprint","IMPRINT",EDGE,{"disambiguationData":[TD([[subQ30,1.0]])],"derivedFrom":subQ24})])]})])],"derivedFrom":subQ15}),makeQuery(id+"F19.boolean.opBoolean","SPLIT",FACE,{"disambiguationData":[TD([makeQuery(id+"F19.opExtrude","SWEPT_FACE",FACE,{"disambiguationData":[OSD([subQ24]),TDD([makeQuery(id+"F18.imprint","IMPRINT",EDGE,{"disambiguationData":[TD([[subQ26,-1.0]])],"derivedFrom":subQ24}),makeQuery(id+"F18.imprint","IMPRINT",EDGE,{"disambiguationData":[TD([[makeQuery(id+"F18.imprint","INTERSECT",VERTEX,{"derivedFrom":[subQ24,subQ4]}),1.0]])],"derivedFrom":subQ24})])]})])],"derivedFrom":subQ15}),makeQuery(id+"F19.boolean.opBoolean","SPLIT",FACE,{"disambiguationData":[TD([makeQuery(id+"F19.opExtrude","SWEPT_FACE",FACE,{"disambiguationData":[OSD([subQ5]),TDD([makeQuery(id+"F18.imprint","IMPRINT",EDGE,{"disambiguationData":[TD([[makeQuery(id+"F18.imprint","INTERSECT",VERTEX,{"derivedFrom":[subQ5,subQ21]}),-1.0]])],"derivedFrom":subQ5}),makeQuery(id+"F18.imprint","IMPRINT",EDGE,{"disambiguationData":[TD([[subQ18,1.0]])],"derivedFrom":subQ5})])]})])],"derivedFrom":subQ15}),makeQuery(id+"F19.boolean.opBoolean","SPLIT",FACE,{"disambiguationData":[TD([makeQuery(id+"F19.opExtrude","SWEPT_FACE",FACE,{"disambiguationData":[OSD([subQ5]),TDD([makeQuery(id+"F18.imprint","IMPRINT",EDGE,{"disambiguationData":[TD([[subQ9,-1.0]])],"derivedFrom":subQ5}),makeQuery(id+"F18.imprint","IMPRINT",EDGE,{"disambiguationData":[TD([[makeQuery(id+"F18.imprint","INTERSECT",VERTEX,{"derivedFrom":[subQ5,subQ4]}),1.0]])],"derivedFrom":subQ5})])]})])],"derivedFrom":subQ15}),makeQuery(id+"F55.opExtrude","CAP_FACE",FACE,{"disambiguationData":[OSD([sQuery(id+"F54.wireOp",EDGE,"E41.bottom"),sQuery(id+"F54.wireOp",EDGE,"E41.top"),sQuery(id+"F54.wireOp",EDGE,"E41.left"),sQuery(id+"F54.wireOp",EDGE,"E41.right"),sQuery(id+"F54.wireOp",EDGE,"E42.bottom"),sQuery(id+"F54.wireOp",EDGE,"E42.top"),sQuery(id+"F54.wireOp",EDGE,"E42.left"),sQuery(id+"F54.wireOp",EDGE,"E42.right")])],"isStart":false})]});}
            var sketch = newSketch(context, id + "F57", { "sketchPlane" : qUnion([Q0])});
            skLineSegment(sketch, "E43.bottom", {"start": v(22.5, 22.5) * mm, "end": v(-22.5, 22.5) * mm});
            skLineSegment(sketch, "E43.top", {"start": v(22.5, -22.5) * mm, "end": v(-22.5, -22.5) * mm});
            skLineSegment(sketch, "E43.left", {"start": v(22.5, 22.5) * mm, "end": v(22.5, -22.5) * mm});
            skLineSegment(sketch, "E43.right", {"start": v(-22.5, 22.5) * mm, "end": v(-22.5, -22.5) * mm});
            skPoint(sketch, "E43.middle", {"position": v(0, 0) * mm});
            skSolve(sketch);
        }
        {
            var Q0;
            Q0=makeQuery(id+"F57.imprint","IMPRINT",FACE,{"disambiguationData":[TD([[makeQuery(id+"F57.imprint","IMPRINT",EDGE,{"derivedFrom":sQuery(id+"F57.wireOp",EDGE,"E43.bottom")}),1.0]])]});
            extrude(context, id + "F58", {"entities" : qUnion([Q0]), "operationType" : NewBodyOperationType.ADD, "depth" : 16 * mm});
        }
        {
            var Q0;
            Q0=makeQuery(id+"F58.opExtrude","CAP_FACE",FACE,{"disambiguationData":[OSD([sQuery(id+"F57.wireOp",EDGE,"E43.bottom"),sQuery(id+"F57.wireOp",EDGE,"E43.top"),sQuery(id+"F57.wireOp",EDGE,"E43.left"),sQuery(id+"F57.wireOp",EDGE,"E43.right")])],"isStart":false});
            var sketch = newSketch(context, id + "F59", { "sketchPlane" : qUnion([Q0])});
            skLineSegment(sketch, "E44.bottom", {"start": v(23.5, 23.5) * mm, "end": v(-23.5, 23.5) * mm});
            skLineSegment(sketch, "E44.top", {"start": v(23.5, -23.5) * mm, "end": v(-23.5, -23.5) * mm});
            skLineSegment(sketch, "E44.left", {"start": v(23.5, 23.5) * mm, "end": v(23.5, -23.5) * mm});
            skLineSegment(sketch, "E44.right", {"start": v(-23.5, 23.5) * mm, "end": v(-23.5, -23.5) * mm});
            skPoint(sketch, "E44.middle", {"position": v(0, 0) * mm});
            skSolve(sketch);
        }
        {
            var Q0;
            Q0 = qSketchRegion(id + "F59", true);
            extrude(context, id + "F60", {"entities" : qUnion([Q0]), "operationType" : NewBodyOperationType.ADD, "depth" : 16 * mm});
        }
        {
            var Q0;
            Q0=makeQuery(id+"F58.opExtrude","SWEPT_FACE",FACE,{"disambiguationData":[OSD([sQuery(id+"F57.wireOp",EDGE,"E43.top")])]});
            var sketch = newSketch(context, id + "F61", { "sketchPlane" : qUnion([Q0])});
            skLineSegment(sketch, "E45.bottom", {"start": v(-5, 144) * mm, "end": v(5, 144) * mm});
            skLineSegment(sketch, "E45.top", {"start": v(-5, 156) * mm, "end": v(5, 156) * mm});
            skLineSegment(sketch, "E45.left", {"start": v(-5, 144) * mm, "end": v(-5, 156) * mm});
            skLineSegment(sketch, "E45.right", {"start": v(5, 144) * mm, "end": v(5, 156) * mm});
            skLineSegment(sketch, "E46.bottom", {"start": v(-13, 144) * mm, "end": v(-8, 144) * mm});
            skLineSegment(sketch, "E46.top", {"start": v(-13, 156) * mm, "end": v(-8, 156) * mm});
            skLineSegment(sketch, "E46.left", {"start": v(-13, 144) * mm, "end": v(-13, 156) * mm});
            skLineSegment(sketch, "E46.right", {"start": v(-8, 144) * mm, "end": v(-8, 156) * mm});
            skLineSegment(sketch, "E47.bottom", {"start": v(8, 144) * mm, "end": v(13, 144) * mm});
            skLineSegment(sketch, "E47.top", {"start": v(8, 156) * mm, "end": v(13, 156) * mm});
            skLineSegment(sketch, "E47.left", {"start": v(8, 144) * mm, "end": v(8, 156) * mm});
            skLineSegment(sketch, "E47.right", {"start": v(13, 144) * mm, "end": v(13, 156) * mm});
            skSolve(sketch);
        }
        {
            var Q0;
            Q0=makeQuery(id+"F61.imprint","IMPRINT",FACE,{"disambiguationData":[TD([[makeQuery(id+"F61.imprint","IMPRINT",EDGE,{"derivedFrom":sQuery(id+"F61.wireOp",EDGE,"E45.bottom")}),-1.0]])]});
            extrude(context, id + "F62", {"entities" : qUnion([Q0]), "operationType" : NewBodyOperationType.REMOVE, "endBound" : BoundingType.THROUGH_ALL, "oppositeDirection" : true, "depth" : 25 * mm});
        }
        {
            var Q0;
            Q0=makeQuery(id+"F61.imprint","IMPRINT",FACE,{"disambiguationData":[TD([[makeQuery(id+"F61.imprint","IMPRINT",EDGE,{"derivedFrom":sQuery(id+"F61.wireOp",EDGE,"E46.bottom")}),-1.0]])]});
            var Q1;
            Q1=makeQuery(id+"F61.imprint","IMPRINT",FACE,{"disambiguationData":[TD([[makeQuery(id+"F61.imprint","IMPRINT",EDGE,{"derivedFrom":sQuery(id+"F61.wireOp",EDGE,"E47.bottom")}),-1.0]])]});
            extrude(context, id + "F63", {"entities" : qUnion([Q0, Q1]), "operationType" : NewBodyOperationType.REMOVE, "oppositeDirection" : true, "depth" : 10 * mm});
        }
        {
            var Q0;
            Q0=makeQuery(id+"F58.opExtrude","SWEPT_FACE",FACE,{"disambiguationData":[OSD([sQuery(id+"F57.wireOp",EDGE,"E43.right")])]});
            var sketch = newSketch(context, id + "F64", { "sketchPlane" : qUnion([Q0])});
            skLineSegment(sketch, "E48.bottom", {"start": v(-5, 144) * mm, "end": v(5, 144) * mm});
            skLineSegment(sketch, "E48.top", {"start": v(-5, 156) * mm, "end": v(5, 156) * mm});
            skLineSegment(sketch, "E48.left", {"start": v(-5, 144) * mm, "end": v(-5, 156) * mm});
            skLineSegment(sketch, "E48.right", {"start": v(5, 144) * mm, "end": v(5, 156) * mm});
            skPoint(sketch, "E49", {"position": v(-22.5, 144) * mm});
            skSolve(sketch);
        }
        {
            var Q0;
            Q0=makeQuery(id+"F64.imprint","IMPRINT",FACE,{"disambiguationData":[TD([[makeQuery(id+"F64.imprint","IMPRINT",EDGE,{"derivedFrom":sQuery(id+"F64.wireOp",EDGE,"E48.bottom")}),1.0]])]});
            extrude(context, id + "F65", {"entities" : qUnion([Q0]), "operationType" : NewBodyOperationType.REMOVE, "endBound" : BoundingType.THROUGH_ALL, "oppositeDirection" : true, "depth" : 25 * mm});
        }
    });
